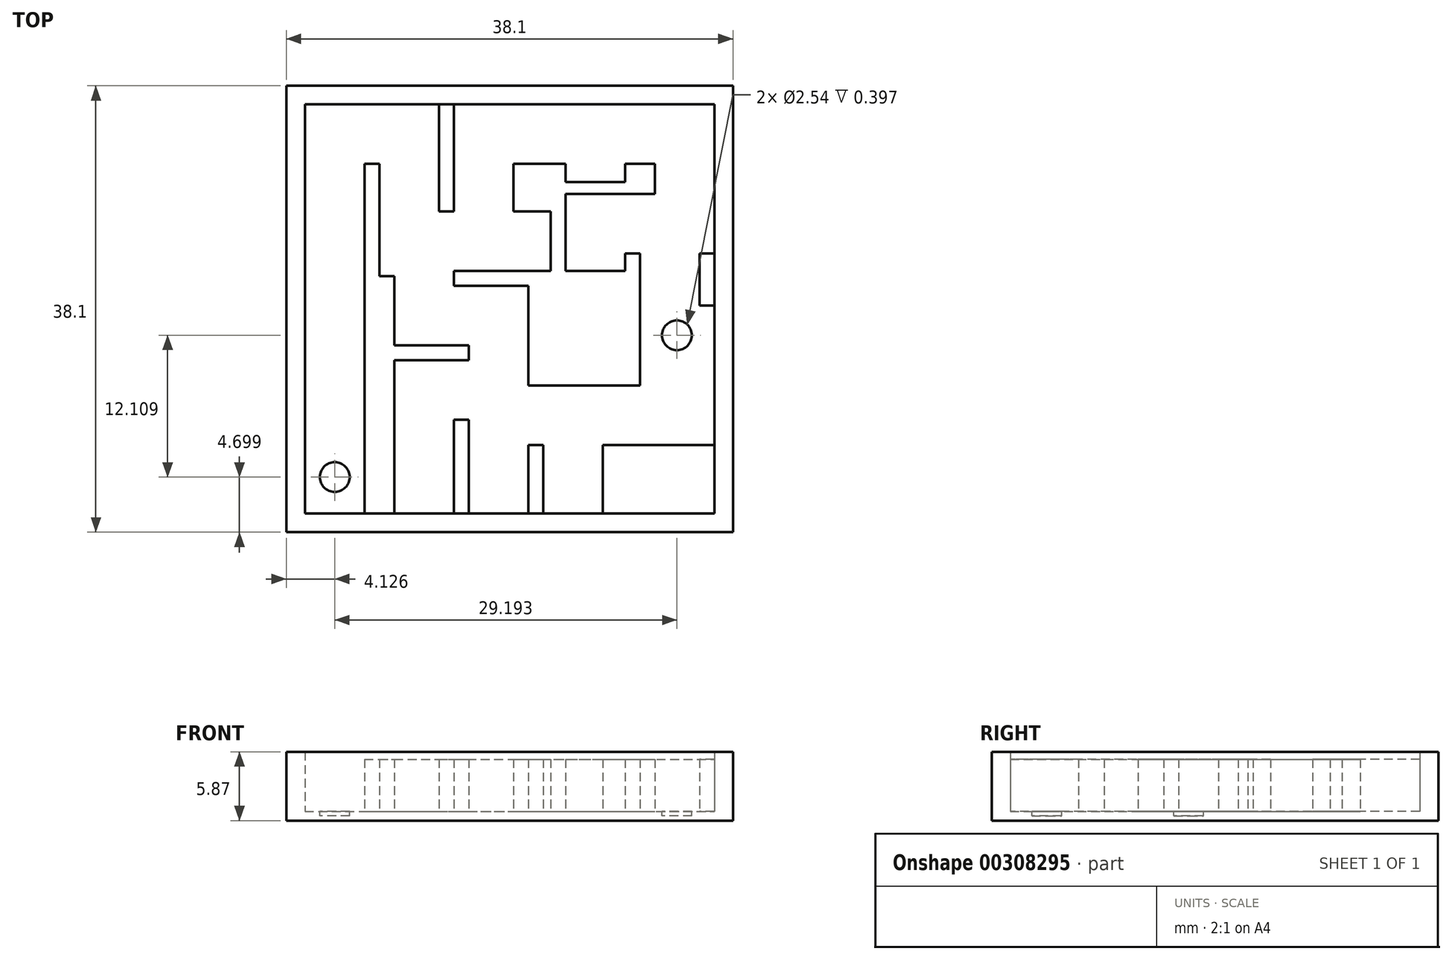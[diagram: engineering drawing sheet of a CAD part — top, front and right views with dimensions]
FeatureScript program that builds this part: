
annotation { "Feature Type Name" : "Feature", "Feature Type Description" : "" }
export const myFeature = defineFeature(function(context is Context, id is Id, definition is map)
    precondition{}
    {
        {
            var Q0;
            Q0=qCreatedBy(makeId("Top.planeOp"),FACE);
            var sketch = newSketch(context, id + "F0", { "sketchPlane" : qUnion([Q0])});
            skLineSegment(sketch, "E0.bottom", {"start": v(-19.1, 22.5) * mm, "end": v(19, 22.5) * mm});
            skLineSegment(sketch, "E0.top", {"start": v(-19.1, -15.6) * mm, "end": v(19, -15.6) * mm});
            skLineSegment(sketch, "E0.left", {"start": v(-19.1, 22.5) * mm, "end": v(-19.1, -15.6) * mm});
            skLineSegment(sketch, "E0.right", {"start": v(19, 22.5) * mm, "end": v(19, -15.6) * mm});
            skSolve(sketch);
        }
        {
            var Q0;
            Q0=makeQuery(id+"F0.imprint","IMPRINT",FACE,{"disambiguationData":[TD([[makeQuery(id+"F0.imprint","IMPRINT",EDGE,{"derivedFrom":sQuery(id+"F0.wireOp",EDGE,"E0.bottom")}),-1.0]])]});
            extrude(context, id + "F1", {"entities" : qUnion([Q0]), "depth" : 0.8 * mm});
        }
        {
            var Q0;
            Q0=makeQuery(id+"F1.opExtrude","CAP_FACE",FACE,{"disambiguationData":[OSD([sQuery(id+"F0.wireOp",EDGE,"E0.bottom"),sQuery(id+"F0.wireOp",EDGE,"E0.top"),sQuery(id+"F0.wireOp",EDGE,"E0.left"),sQuery(id+"F0.wireOp",EDGE,"E0.right")])],"isStart":false});
            var sketch = newSketch(context, id + "F2", { "sketchPlane" : qUnion([Q0])});
            skLineSegment(sketch, "E1.0", {"start": v(-17.5, 20.92) * mm, "end": v(17.42, 20.92) * mm});
            skLineSegment(sketch, "E1.1", {"start": v(-17.5, 20.92) * mm, "end": v(-17.5, -14) * mm});
            skLineSegment(sketch, "E1.2", {"start": v(-17.5, -14) * mm, "end": v(17.42, -14) * mm});
            skLineSegment(sketch, "E1.3", {"start": v(17.42, 20.92) * mm, "end": v(17.42, -14) * mm});
            skSolve(sketch);
        }
        {
            var Q0;
            Q0=makeQuery(id+"F2.imprint","IMPRINT",FACE,{"disambiguationData":[TD([[makeQuery(id+"F2.imprint","IMPRINT",EDGE,{"derivedFrom":sQuery(id+"F2.wireOp",EDGE,"E1.0")}),1.0]])]});
            extrude(context, id + "F3", {"entities" : qUnion([Q0]), "operationType" : NewBodyOperationType.ADD, "depth" : 5.08 * mm});
        }
        {
            var Q0;
            Q0=makeQuery(id+"F1.opExtrude","CAP_FACE",FACE,{"disambiguationData":[OSD([sQuery(id+"F0.wireOp",EDGE,"E0.bottom"),sQuery(id+"F0.wireOp",EDGE,"E0.top"),sQuery(id+"F0.wireOp",EDGE,"E0.left"),sQuery(id+"F0.wireOp",EDGE,"E0.right")])],"isStart":false});
            var sketch = newSketch(context, id + "F4", { "sketchPlane" : qUnion([Q0])});
            skLineSegment(sketch, "E2.top", {"start": v(-12.42, 15.84) * mm, "end": v(-11.15, 15.84) * mm});
            skLineSegment(sketch, "E2.left", {"start": v(-12.42, -14) * mm, "end": v(-12.42, 15.84) * mm});
            skLineSegment(sketch, "E2.right", {"start": v(-11.15, 6.26) * mm, "end": v(-11.15, 15.84) * mm});
            skLineSegment(sketch, "E3.top", {"start": v(-6.07, 11.77) * mm, "end": v(-4.8, 11.77) * mm});
            skLineSegment(sketch, "E3.left", {"start": v(-6.07, 20.92) * mm, "end": v(-6.07, 11.77) * mm});
            skLineSegment(sketch, "E3.right", {"start": v(-4.8, 20.92) * mm, "end": v(-4.8, 11.77) * mm});
            skLineSegment(sketch, "E4.bottom", {"start": v(-11.15, 6.26) * mm, "end": v(-9.88, 6.26) * mm});
            skLineSegment(sketch, "E4.right", {"start": v(-9.88, 6.26) * mm, "end": v(-9.88, 0.34) * mm});
            skLineSegment(sketch, "E5.bottom", {"start": v(-4.8, 6.69) * mm, "end": v(3.45, 6.69) * mm});
            skLineSegment(sketch, "E5.top", {"start": v(-4.8, 5.42) * mm, "end": v(1.55, 5.42) * mm});
            skLineSegment(sketch, "E5.left", {"start": v(-4.8, 6.69) * mm, "end": v(-4.8, 5.42) * mm});
            skLineSegment(sketch, "E6.bottom", {"start": v(0.28, 15.84) * mm, "end": v(1.55, 15.84) * mm});
            skLineSegment(sketch, "E6.top", {"start": v(0.28, 11.77) * mm, "end": v(1.55, 11.77) * mm});
            skLineSegment(sketch, "E6.left", {"start": v(0.28, 15.84) * mm, "end": v(0.28, 11.77) * mm});
            skLineSegment(sketch, "E7.top", {"start": v(3.45, 15.84) * mm, "end": v(4.72, 15.84) * mm});
            skLineSegment(sketch, "E7.left", {"start": v(3.45, 6.69) * mm, "end": v(3.45, 11.77) * mm});
            skLineSegment(sketch, "E7.right", {"start": v(4.72, 6.69) * mm, "end": v(4.72, 13.27) * mm});
            skLineSegment(sketch, "E8.bottom", {"start": v(4.72, 14.29) * mm, "end": v(9.8, 14.29) * mm});
            skLineSegment(sketch, "E8.top", {"start": v(4.72, 13.27) * mm, "end": v(12.34, 13.27) * mm});
            skLineSegment(sketch, "E8.right", {"start": v(12.34, 14.29) * mm, "end": v(12.34, 13.27) * mm});
            skLineSegment(sketch, "E9.top", {"start": v(9.8, 15.84) * mm, "end": v(12.34, 15.84) * mm});
            skLineSegment(sketch, "E9.left", {"start": v(9.8, 14.29) * mm, "end": v(9.8, 15.84) * mm});
            skLineSegment(sketch, "E9.right", {"start": v(12.34, 14.29) * mm, "end": v(12.34, 15.84) * mm});
            skLineSegment(sketch, "E10.top", {"start": v(9.8, 8.2) * mm, "end": v(11.07, 8.2) * mm});
            skLineSegment(sketch, "E10.left", {"start": v(9.8, 6.69) * mm, "end": v(9.8, 8.2) * mm});
            skLineSegment(sketch, "E10.right", {"start": v(11.07, 5.15) * mm, "end": v(11.07, 8.2) * mm});
            skLineSegment(sketch, "E11.trimOffspring", {"start": v(4.72, 14.29) * mm, "end": v(4.72, 15.84) * mm});
            skLineSegment(sketch, "E12.trimOffspring", {"start": v(4.72, 6.69) * mm, "end": v(9.8, 6.69) * mm});
            skLineSegment(sketch, "E13", {"start": v(1.55, 11.77) * mm, "end": v(3.45, 11.77) * mm});
            skLineSegment(sketch, "E14", {"start": v(1.55, 15.84) * mm, "end": v(3.45, 15.84) * mm});
            skLineSegment(sketch, "E15", {"start": v(11.07, 5.42) * mm, "end": v(11.07, 5.15) * mm});
            skLineSegment(sketch, "E16.bottom", {"start": v(17.42, 8.2) * mm, "end": v(16.15, 8.2) * mm});
            skLineSegment(sketch, "E16.top", {"start": v(17.42, 3.75) * mm, "end": v(16.15, 3.75) * mm});
            skLineSegment(sketch, "E16.right", {"start": v(16.15, 8.2) * mm, "end": v(16.15, 3.75) * mm});
            skLineSegment(sketch, "E17.bottom", {"start": v(-9.88, 0.34) * mm, "end": v(-3.53, 0.34) * mm});
            skLineSegment(sketch, "E17.top", {"start": v(-9.88, -0.93) * mm, "end": v(-3.53, -0.93) * mm});
            skLineSegment(sketch, "E17.right", {"start": v(-3.53, 0.34) * mm, "end": v(-3.53, -0.93) * mm});
            skLineSegment(sketch, "E18.left", {"start": v(1.55, 5.42) * mm, "end": v(1.55, -3.1) * mm});
            skLineSegment(sketch, "E19.bottom", {"start": v(-4.8, -14) * mm, "end": v(-3.53, -14) * mm});
            skLineSegment(sketch, "E19.top", {"start": v(-4.8, -6.01) * mm, "end": v(-3.53, -6.01) * mm});
            skLineSegment(sketch, "E19.left", {"start": v(-4.8, -14) * mm, "end": v(-4.8, -6.01) * mm});
            skLineSegment(sketch, "E19.right", {"start": v(-3.53, -14) * mm, "end": v(-3.53, -6.01) * mm});
            skLineSegment(sketch, "E20.top", {"start": v(7.9, -8.18) * mm, "end": v(17.42, -8.18) * mm});
            skLineSegment(sketch, "E20.left", {"start": v(7.9, -14) * mm, "end": v(7.9, -8.18) * mm});
            skLineSegment(sketch, "E21.right", {"start": v(11.07, -3.1) * mm, "end": v(11.07, 5.15) * mm});
            skLineSegment(sketch, "E22", {"start": v(1.55, -3.1) * mm, "end": v(11.07, -3.1) * mm});
            skLineSegment(sketch, "E23", {"start": v(1.55, -14) * mm, "end": v(1.55, -8.18) * mm});
            skLineSegment(sketch, "E24", {"start": v(1.55, -8.18) * mm, "end": v(2.82, -8.18) * mm});
            skLineSegment(sketch, "E25", {"start": v(2.82, -8.18) * mm, "end": v(2.82, -14) * mm});
            skLineSegment(sketch, "E26.bottom", {"start": v(16.15, -8.18) * mm, "end": v(17.42, -8.18) * mm});
            skLineSegment(sketch, "E26.top", {"start": v(16.15, -3.2) * mm, "end": v(17.42, -3.2) * mm});
            skLineSegment(sketch, "E26.left", {"start": v(16.15, -8.18) * mm, "end": v(16.15, -3.2) * mm});
            skCircle(sketch, "E27", {"center": v(14.23, 1.2) * mm, "radius": 1.27 * mm});
            skLineSegment(sketch, "E28", {"start": v(-17.5, -14) * mm, "end": v(-12.42, -14) * mm});
            skCircle(sketch, "E29", {"center": v(-14.96, -10.9) * mm, "radius": 1.27 * mm});
            skPoint(sketch, "E29.centerSnap0", {"position": v(-14.96, -14) * mm});
            skLineSegment(sketch, "E30.trimOffspring", {"start": v(-9.88, -0.93) * mm, "end": v(-9.88, -14) * mm});
            skSolve(sketch);
        }
        {
            var Q0;
            Q0=makeQuery(id+"F4.imprint","IMPRINT",FACE,{"disambiguationData":[TD([[makeQuery(id+"F4.imprint","IMPRINT",EDGE,{"derivedFrom":sQuery(id+"F4.wireOp",EDGE,"E2.bottom")}),1.0]])]});
            var Q1;
            Q1=makeQuery(id+"F4.imprint","IMPRINT",FACE,{"disambiguationData":[TD([[makeQuery(id+"F4.imprint","IMPRINT",EDGE,{"derivedFrom":sQuery(id+"F4.wireOp",EDGE,"E3.bottom")}),-1.0]])]});
            var Q2;
            Q2=makeQuery(id+"F4.imprint","IMPRINT",FACE,{"disambiguationData":[TD([[makeQuery(id+"F4.imprint","IMPRINT",EDGE,{"derivedFrom":sQuery(id+"F4.wireOp",EDGE,"E5.bottom")}),-1.0]])]});
            var Q3;
            Q3=makeQuery(id+"F4.imprint","IMPRINT",FACE,{"disambiguationData":[TD([[makeQuery(id+"F4.imprint","IMPRINT",EDGE,{"derivedFrom":sQuery(id+"F4.wireOp",EDGE,"E16.bottom")}),1.0]])]});
            extrude(context, id + "F5", {"entities" : qUnion([Q0, Q1, Q2, Q3]), "operationType" : NewBodyOperationType.ADD, "depth" : 4.44 * mm});
        }
        {
            var Q0;
            Q0=makeQuery(id+"F4.imprint","IMPRINT",FACE,{"disambiguationData":[TD([[makeQuery(id+"F4.imprint","IMPRINT",EDGE,{"derivedFrom":sQuery(id+"F4.wireOp",EDGE,"E2.top")}),-1.0]])]});
            var Q1;
            Q1=makeQuery(id+"F4.imprint","IMPRINT",FACE,{"disambiguationData":[TD([[makeQuery(id+"F4.imprint","IMPRINT",EDGE,{"derivedFrom":sQuery(id+"F4.wireOp",EDGE,"E19.bottom")}),1.0]])]});
            var Q2;
            {var subQ0=sQuery(id+"F4.wireOp",EDGE,"E23");Q2=makeQuery(id+"F4.imprint","IMPRINT",FACE,{"disambiguationData":[TD([[makeQuery(id+"F4.imprint","IMPRINT",EDGE,{"derivedFrom":subQ0}),-1.0]])]});}
            var Q3;
            Q3=makeQuery(id+"F4.imprint","IMPRINT",FACE,{"disambiguationData":[TD([[makeQuery(id+"F4.imprint","IMPRINT",EDGE,{"derivedFrom":sQuery(id+"F4.wireOp",EDGE,"E20.top")}),-1.0]])]});
            var Q4;
            {var subQ0=sQuery(id+"F4.wireOp",EDGE,"E26.bottom");Q4=makeQuery(id+"F4.imprint","IMPRINT",FACE,{"disambiguationData":[TD([[makeQuery(id+"F4.imprint","IMPRINT",EDGE,{"derivedFrom":subQ0}),1.0]])]});}
            var Q5;
            Q5=makeQuery(id+"F4.imprint","IMPRINT",FACE,{"disambiguationData":[TD([[makeQuery(id+"F4.imprint","IMPRINT",EDGE,{"derivedFrom":sQuery(id+"F4.wireOp",EDGE,"E3.top")}),1.0]])]});
            extrude(context, id + "F6", {"entities" : qUnion([Q0, Q1, Q2, Q3, Q4, Q5]), "operationType" : NewBodyOperationType.ADD, "depth" : 4.44 * mm});
        }
        {
            var Q0;
            Q0=makeQuery(id+"F4.imprint","IMPRINT",FACE,{"disambiguationData":[TD([[makeQuery(id+"F4.imprint","IMPRINT",EDGE,{"derivedFrom":sQuery(id+"F4.wireOp",EDGE,"E29")}),1.0]])]});
            extrude(context, id + "F7", {"entities" : qUnion([Q0]), "operationType" : NewBodyOperationType.REMOVE, "oppositeDirection" : true, "depth" : 0.4 * mm});
        }
        {
            var Q0;
            Q0=makeQuery(id+"F4.imprint","IMPRINT",FACE,{"disambiguationData":[TD([[makeQuery(id+"F4.imprint","IMPRINT",EDGE,{"derivedFrom":sQuery(id+"F4.wireOp",EDGE,"E27")}),1.0]])]});
            extrude(context, id + "F8", {"entities" : qUnion([Q0]), "operationType" : NewBodyOperationType.REMOVE, "oppositeDirection" : true, "depth" : 0.4 * mm});
        }
    });
